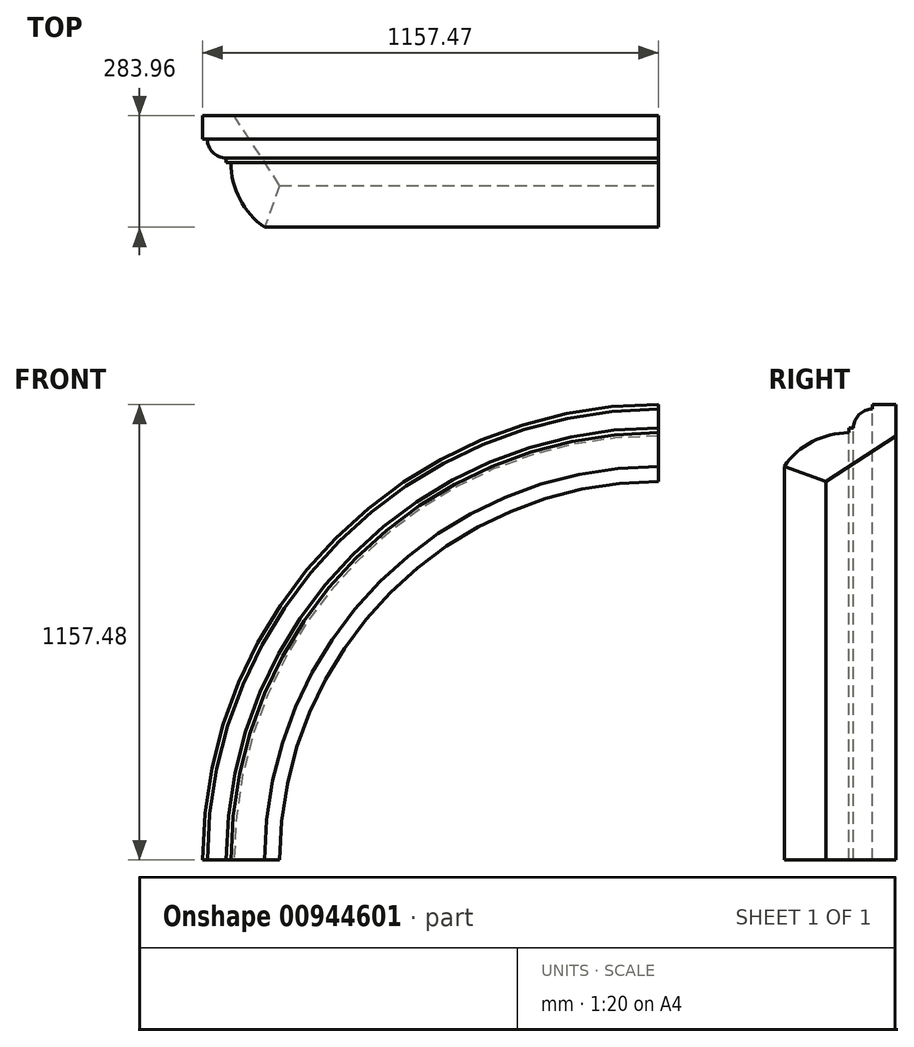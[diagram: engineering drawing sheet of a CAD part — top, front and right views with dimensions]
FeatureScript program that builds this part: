
annotation { "Feature Type Name" : "Feature", "Feature Type Description" : "" }
export const myFeature = defineFeature(function(context is Context, id is Id, definition is map)
    precondition{}
    {
        {
            var Q0;
            Q0=qCreatedBy(makeId("Top.planeOp"),FACE);
            var sketch = newSketch(context, id + "F0", { "sketchPlane" : qUnion([Q0])});
            skLineSegment(sketch, "E0", {"start": v(0, 0) * mm, "end": v(-115.87, 178.12) * mm});
            skLineSegment(sketch, "E1", {"start": v(-115.87, 178.12) * mm, "end": v(-195.87, 178.12) * mm});
            skLineSegment(sketch, "E2", {"start": v(-195.87, 178.12) * mm, "end": v(-195.87, 118.12) * mm});
            skLineSegment(sketch, "E3", {"start": v(-195.87, 118.12) * mm, "end": v(-183.87, 118.12) * mm});
            skLineSegment(sketch, "E4", {"start": v(0, 0) * mm, "end": v(-38.4, -105.84) * mm});
            skLineSegment(sketch, "E5", {"start": v(-183.87, 118.12) * mm, "end": v(-135.87, 118.12) * mm, "construction": true});
            skArc(sketch, "E6", {"start": v(-183.87, 118.12) * mm, "mid": v(-169.82, 84.18) * mm, "end": v(-135.87, 70.12) * mm});
            skLineSegment(sketch, "E7", {"start": v(-135.87, 70.12) * mm, "end": v(-135.87, 58.12) * mm});
            skLineSegment(sketch, "E8", {"start": v(-135.87, 58.12) * mm, "end": v(-123.87, 58.12) * mm});
            skLineSegment(sketch, "E9", {"start": v(-123.87, 58.12) * mm, "end": v(76.13, 58.12) * mm, "construction": true});
            skArc(sketch, "E10", {"start": v(-123.87, 58.12) * mm, "mid": v(-101.22, -34.33) * mm, "end": v(-38.4, -105.84) * mm});
            skLineSegment(sketch, "E11", {"start": v(76.13, 58.12) * mm, "end": v(7.92, -129.89) * mm, "construction": true});
            skSolve(sketch);
        }
        {
            var Q0;
            Q0=qCreatedBy(makeId("Front.planeOp"),FACE);
            var Q1;
            Q1=sQuery(id+"F0.wireOp",VERTEX,"E4.end");
            cPlane(context, id + "F1", {"entities" : qUnion([Q0, Q1]), "cplaneType" : CPlaneType.PLANE_POINT, "offset" : 104 * mm, "width" : 150 * mm, "height" : 150 * mm});
        }
        {
            var Q0;
            Q0=qCreatedBy(id+"F1.planeOp",FACE);
            var sketch = newSketch(context, id + "F2", { "sketchPlane" : qUnion([Q0])});
            skPoint(sketch, "E12.0", {"position": v(-38.4, 0) * mm});
            skLineSegment(sketch, "E13", {"start": v(-38.4, 0) * mm, "end": v(961.6, 0) * mm, "construction": true});
            skArc(sketch, "E14", {"start": v(-38.4, 0) * mm, "mid": v(254.5, 707.1) * mm, "end": v(961.6, 1000) * mm});
            skLineSegment(sketch, "E15", {"start": v(961.6, 0) * mm, "end": v(961.6, 1000) * mm, "construction": true});
            skSolve(sketch);
        }
        {
            var Q0;
            Q0 = qSketchRegion(id + "F0", true);
            var Q1;
            Q1 = qConstructionFilter(qBodyType(qCreatedBy(id + "F2" ,EDGE), BodyType.WIRE), ConstructionObject.NO);
            sweep(context, id + "F3", {"profiles" : qUnion([Q0]), "path" : qUnion([Q1])});
        }
    });
